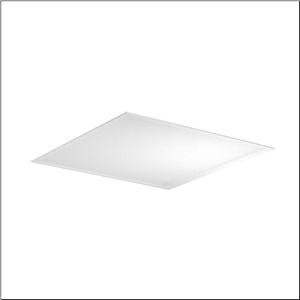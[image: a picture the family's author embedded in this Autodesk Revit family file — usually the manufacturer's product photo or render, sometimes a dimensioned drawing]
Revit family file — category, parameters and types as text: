
# Revit family: apollon_r__21_square_51mq12wd2414_a4f3
name_source: partatom
category: Lighting Fixtures
units: mm (PartAtom-declared; Revit-internal decimal feet)

## family parameters
Cut with Voids When Loaded = No
Host = Face
Light Source = No
Part Type = Normal
Room Calculation Point = No
Round Connector Dimension = Use Diameter
Shared = No

## types (1)
- Apollon® 21 square (1 x LED, 4200 lm, 24.7 W, 4000K)
    Apparent Load = 25 VA
    CIE Flux Codes = 60 87 97 100 100
    Color Rendering = 80
    Color Temperature = 4000K
    Default Elevation = 1800 mm
    Description = Apollon® 21 square, office luminaire, primary optical cover: micro prismatic cover, of PMMA, CAT 2 (L<= 3000cd/m²), light emission: direct distribution, primary light characteristic: symmetric, installation type: lay-in mounting, LED, rated luminous flux: 4.200lm, luminous efficacy: 170lm/W, light colour: 840, colour temperature: 4000K, with terminal, 5-pole, mains connection: 220..240V, AC/DC, 0/50..60Hz, rated input power: 24.7W, housing, of aluminium, coated, traffic white (RAL 9016), module: M600, length: 595mm, width: 595mm, height: 30mm, housing upper side, of sheet steel, galvanised, protection rating (complete): IP20, protection rating (lamp compartment, on room side): IP50, insulation class (complete): insulation class II (safety insulation), certification: CE, ENEC, impact resistance: IK03, permissible operating ambient temperature: -20..+45°C, permissible storage temperature: -40..+80°C, packaging unit: 1 piece
    Height = 0 mm  [stored 0 ft]
    Lamp = 1 x LED
    Lamp Light Flux = 4200 lm
    Lamp Power = 24.7 W
    Lamp count = 1
    Length = 595 mm
    Luminous efficacy = 170 lm/W
    Manufacturer = Siteco
    ModVariant = No
    Model = 51MQ12WD2414
    Mounting Place = Ceiling
    Mounting Type = Recessed
    Number of Poles = 1
    OnlyDefault = Yes
    Power Factor = 1
    Product Name = Apollon® 21 square
    Product group = office luminaire | ceiling recessed
    ProductGroupID = 401
    Protection Class = Protection class II
    Protection Degree = IP 20
    RLX_Detail_Level = 1
    RLX_Emergency_Light_Flux = 0 lm
    RLX_Emergency_Type = 0
    RLX_Emergency_Type_DB = No
    RlxData = <blob elided: 12493 chars, md5=39e3156c>
    Socket = socket
    Standby Power = 0 W
    System Light Flux = 4200 lm
    System Power = 25 W
    Type Comments = Product without accessories
    Type Image = l_1291049.jpg
    URL = http://relux.com
    VarID = ---
    Voltage = 0 V
    Weight = 0.00 kg
    Width = 595 mm

note: [stored X ft] marks values corroborated as IEEE doubles in the binary element streams (Revit-internal decimal feet)

## geometry (parser evidence)
native form markers: Sweep x11
no freeform markers — native parametric forms only
